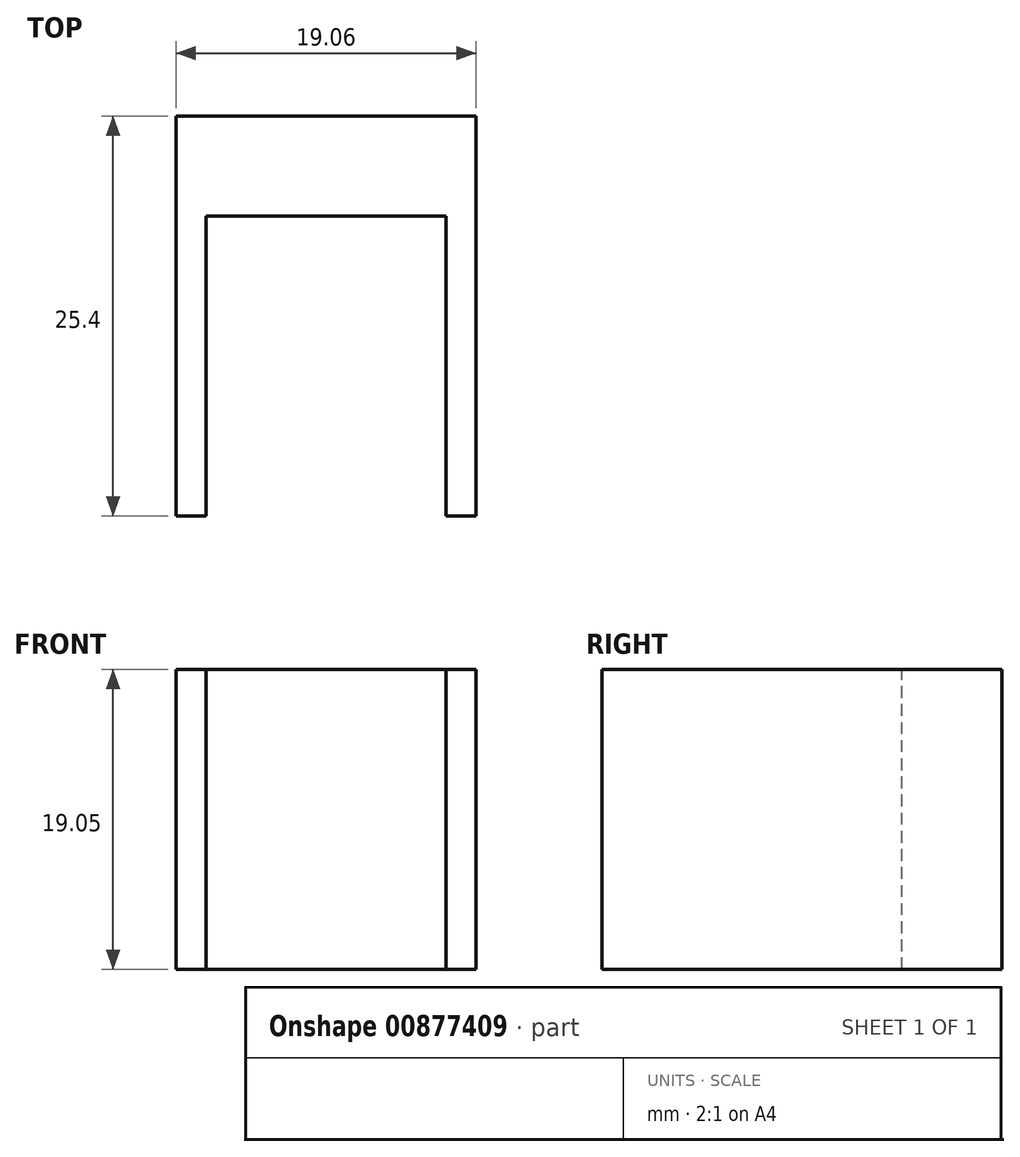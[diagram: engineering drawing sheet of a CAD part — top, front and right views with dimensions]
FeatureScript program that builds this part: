
annotation { "Feature Type Name" : "Feature", "Feature Type Description" : "" }
export const myFeature = defineFeature(function(context is Context, id is Id, definition is map)
    precondition{}
    {
        {
            var Q0;
            Q0=qCreatedBy(makeId("Right.planeOp"),FACE);
            var sketch = newSketch(context, id + "F0", { "sketchPlane" : qUnion([Q0])});
            skLineSegment(sketch, "E0.bottom", {"start": v(-25.4, 19.05) * mm, "end": v(0, 19.05) * mm});
            skLineSegment(sketch, "E0.top", {"start": v(-25.4, 0) * mm, "end": v(0, 0) * mm});
            skLineSegment(sketch, "E0.left", {"start": v(-25.4, 19.05) * mm, "end": v(-25.4, 0) * mm});
            skLineSegment(sketch, "E0.right", {"start": v(0, 19.05) * mm, "end": v(0, 0) * mm});
            skSolve(sketch);
        }
        {
            var Q0;
            Q0=makeQuery(id+"F0.imprint","IMPRINT",FACE,{"disambiguationData":[TD([[makeQuery(id+"F0.imprint","IMPRINT",EDGE,{"derivedFrom":sQuery(id+"F0.wireOp",EDGE,"E0.bottom")}),-1.0]])]});
            extrude(context, id + "F1", {"entities" : qUnion([Q0]), "endBound" : BoundingType.SYMMETRIC, "depth" : 19.05 * mm, "offsetDistance" : 25.4 * mm});
        }
        {
            var Q0;
            Q0=makeQuery(id+"F1.opExtrude","SWEPT_FACE",FACE,{"disambiguationData":[OSD([sQuery(id+"F0.wireOp",EDGE,"E0.left")])]});
            var sketch = newSketch(context, id + "F2", { "sketchPlane" : qUnion([Q0])});
            skLineSegment(sketch, "E1", {"start": v(7.62, 0) * mm, "end": v(7.62, 19.05) * mm});
            skLineSegment(sketch, "E2", {"start": v(-7.63, 19.05) * mm, "end": v(-7.63, 0) * mm});
            skLineSegment(sketch, "E3", {"start": v(-7.63, 0) * mm, "end": v(7.62, 0) * mm});
            skLineSegment(sketch, "E4", {"start": v(-7.63, 19.05) * mm, "end": v(7.62, 19.05) * mm});
            skSolve(sketch);
        }
        {
            var Q0;
            Q0=makeQuery(id+"F2.imprint","IMPRINT",FACE,{"disambiguationData":[TD([[makeQuery(id+"F2.imprint","IMPRINT",EDGE,{"derivedFrom":sQuery(id+"F2.wireOp",EDGE,"y6tsyYup-CaPD-UJ05-NUnn-ROkwPXIl2DAv")}),-1.0]])]});
            var Q1;
            Q1=makeQuery(id+"F2.imprint","IMPRINT",FACE,{"disambiguationData":[TD([[makeQuery(id+"F2.imprint","IMPRINT",EDGE,{"derivedFrom":sQuery(id+"F2.wireOp",EDGE,"E1")}),1.0]])]});
            extrude(context, id + "F3", {"entities" : qUnion([Q0, Q1]), "operationType" : NewBodyOperationType.REMOVE, "oppositeDirection" : true, "depth" : 19.05 * mm, "offsetDistance" : 25.4 * mm});
        }
    });
